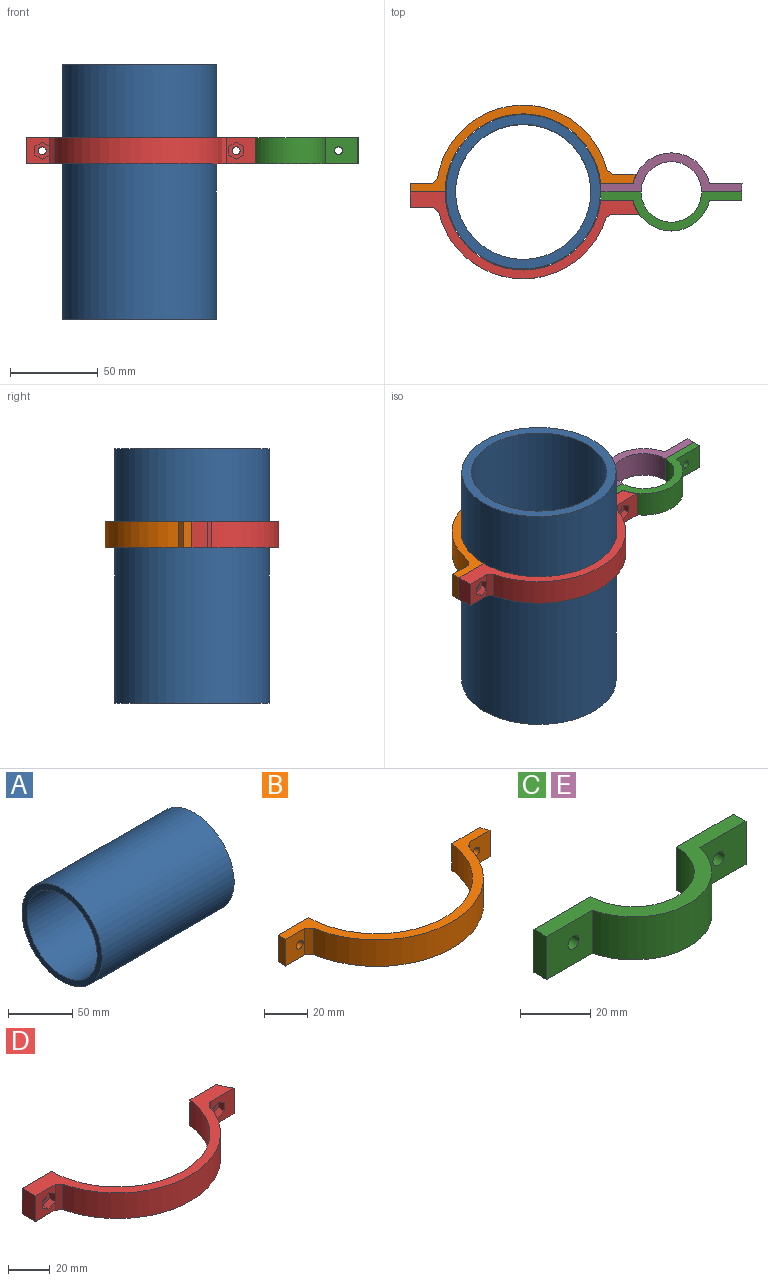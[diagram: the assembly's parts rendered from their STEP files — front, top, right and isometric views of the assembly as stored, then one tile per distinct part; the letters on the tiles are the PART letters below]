
ASSEMBLY  parts=5 mates=6
PART A: 4 faces, bbox 145x88x88 mm
  f0: cylinder r=38.5mm len=145mm, axis (-1,0,0), area 35075.9mm2, adj f2,f3
  f1: cylinder r=44mm len=145mm, axis (-1,0,0), area 40086.7mm2, adj f2,f3
  f2: plane 88x88mm, normal (1,0,0), area 1425.5mm2, adj f0,f1
  f3: plane 88x88mm, normal (-1,0,0), area 1425.5mm2, adj f0,f1
PART B: 14 faces, bbox 128.8x49.5x15 mm
  f0: cylinder r=22.25mm len=15mm, axis (0,0,-1), area 79.9mm2, adj f1,f2,f4,f11
  f1: plane 128.8x49.5mm, normal (0,0,1), area 866.8mm2, adj f0,f4,f5,f6,f7,f8,f9,f11
  f2: plane 128.8x49.5mm, normal (0,0,-1), area 866.8mm2, adj f0,f4,f5,f6,f7,f8,f9,f11
  f3: cylinder r=2.25mm len=5mm, axis (0,1,0), area 70.7mm2, adj f4,f11
  f4: plane 18.28x15mm, normal (0,1,0), area 258.3mm2, adj f0,f1,f2,f3,f5
  f5: cylinder r=44.5mm len=88.72mm, axis (0,0,-1), area 2021.9mm2, adj f1,f2,f4,f6
  f6: plane 20x15mm, normal (0,1,0), area 284.1mm2, adj f1,f2,f5,f7,f10
  f7: plane 15x5mm, normal (-1,0,0), area 75mm2, adj f1,f2,f6,f8
  f8: plane 15x12.55mm, normal (0,-1,0), area 172.4mm2, adj f1,f2,f7,f10,f12
  f9: cylinder r=49.5mm len=96.86mm, axis (0,0,-1), area 2031.7mm2, adj f1,f2,f12,f13
  f10: cylinder r=2.25mm len=5mm, axis (0,1,0), area 70.7mm2, adj f6,f8
  f11: plane 15x13.39mm, normal (0,-1,0), area 184.9mm2, adj f0,f1,f2,f3,f13
  f12: plane 15x3.03mm, normal (-0.65,-0.76,0), area 59.9mm2, adj f1,f2,f8,f9
  f13: plane 15x2.97mm, normal (0.61,-0.79,0), area 56.4mm2, adj f1,f2,f9,f11
PART C: 12 faces, bbox 80.5x22.3x15 mm
  f0: cylinder r=22.25mm len=43.36mm, axis (0,0,-1), area 897.2mm2, adj f1,f7,f8,f9
  f1: plane 18.57x15mm, normal (0,-1,0), area 262.6mm2, adj f0,f2,f8,f9,f11
  f2: cylinder r=89mm len=15mm, axis (0,0,-1), area 75mm2, adj f1,f3,f8,f9
  f3: plane 22.86x15mm, normal (0,1,0), area 327mm2, adj f2,f4,f8,f9,f11
  f4: cylinder r=17.25mm len=34.5mm, axis (0,0,-1), area 812.9mm2, adj f3,f5,f8,f9
  f5: plane 22.86x15mm, normal (0,1,0), area 327mm2, adj f4,f6,f8,f9,f10
  f6: cylinder r=89mm len=15mm, axis (0,0,-1), area 75mm2, adj f5,f7,f8,f9
  f7: plane 18.57x15mm, normal (0,-1,0), area 262.6mm2, adj f0,f6,f8,f9,f10
  f8: plane 80.5x22.25mm, normal (0,0,1), area 491.2mm2, adj f0,f1,f2,f3,f4,f5,f6,f7
  f9: plane 80.5x22.25mm, normal (0,0,-1), area 491.2mm2, adj f0,f1,f2,f3,f4,f5,f6,f7
  f10: cylinder r=2.25mm len=5mm, axis (0,-1,0), area 70.7mm2, adj f5,f7
  f11: cylinder r=2.25mm len=5mm, axis (0,-1,0), area 70.7mm2, adj f1,f3
PART D: 28 faces, bbox 130.6x49.5x15 mm
  f0: plane 9.64x8.35mm, normal (0,-1,0), area 44.5mm2, adj f11,f19,f20,f21,f22,f23,f24
  f1: plane 16.12x15mm, normal (0,-1,0), area 181.4mm2, adj f3,f9,f10,f13,f14,f15,f16,f17
  f2: cylinder r=2.25mm len=4.5mm, axis (0,1,0), area 56.5mm2, adj f4,f12
  f3: cylinder r=22.25mm len=15mm, axis (0,0,-1), area 132.6mm2, adj f1,f4,f9,f10
  f4: plane 18.28x15mm, normal (0,1,0), area 258.3mm2, adj f2,f3,f5,f9,f10
  f5: cylinder r=44.5mm len=88.72mm, axis (0,0,-1), area 2021.9mm2, adj f4,f6,f9,f10
  f6: plane 20x15mm, normal (0,1,0), area 284.1mm2, adj f5,f7,f9,f10,f11
  f7: plane 15x9mm, normal (-1,0,0), area 135mm2, adj f6,f9,f10,f25
  f8: cylinder r=49.5mm len=95.33mm, axis (0,0,-1), area 1931.4mm2, adj f9,f10,f26,f27
  f9: plane 130.62x49.5mm, normal (0,0,1), area 978.8mm2, adj f1,f3,f4,f5,f6,f7,f8,f25
  f10: plane 130.62x49.5mm, normal (0,0,-1), area 978.8mm2, adj f1,f3,f4,f5,f6,f7,f8,f25
  f11: cylinder r=2.25mm len=5mm, axis (0,1,0), area 70.7mm2, adj f0,f6
  f12: plane 9.64x8.35mm, normal (0,-1,0), area 44.5mm2, adj f2,f13,f14,f15,f16,f17,f18
  f13: plane 4.18x4mm, normal (-0.5,0,-0.87), area 19.3mm2, adj f1,f12,f14,f18
  f14: plane 4.18x4mm, normal (0.5,0,-0.87), area 19.3mm2, adj f1,f12,f13,f15
  f15: plane 4.82x4mm, normal (1,0,0), area 19.3mm2, adj f1,f12,f14,f16
  f16: plane 4.18x4mm, normal (0.5,0,0.87), area 19.3mm2, adj f1,f12,f15,f17
  f17: plane 4.18x4mm, normal (-0.5,0,0.87), area 19.3mm2, adj f1,f12,f16,f18
  f18: plane 4.82x4mm, normal (-1,0,0), area 19.3mm2, adj f1,f12,f13,f17
  f19: plane 4.18x4mm, normal (0.5,0,-0.87), area 19.3mm2, adj f0,f20,f24,f25
  f20: plane 4.18x4.02mm, normal (-0.5,0,-0.87), area 19.3mm2, adj f0,f19,f21,f25,f27
  f21: plane 4.82x4.02mm, normal (-1,0,0), area 19.4mm2, adj f0,f20,f22,f27
  f22: plane 4.18x4.02mm, normal (-0.5,0,0.87), area 19.3mm2, adj f0,f21,f23,f25,f27
  f23: plane 4.18x4mm, normal (0.5,0,0.87), area 19.3mm2, adj f0,f22,f24,f25
  f24: plane 4.82x4mm, normal (1,0,0), area 19.3mm2, adj f0,f19,f23,f25
  f25: plane 15x13.39mm, normal (0,-1,0), area 140.5mm2, adj f7,f9,f10,f19,f20,f22,f23,f24
  f26: plane 15x2.86mm, normal (0.59,-0.81,0), area 53.1mm2, adj f1,f8,f9,f10
  f27: plane 15x2.93mm, normal (-0.62,-0.78,0), area 55.8mm2, adj f8,f9,f10,f20,f21,f22,f25
PART E: same geometry as C
PLACE A rot(axis=(0,1,0),90deg) t=(-79.78,-0.5,22.74)mm
PLACE B rot(axis=(1,0,0),180deg) t=(-79.78,-0.5,46.23)mm
PLACE C t=(4.66,-0.5,46.23)mm
PLACE D t=(-79.78,-0.5,46.23)mm
PLACE E rot(axis=(0,0,-1),180deg) t=(4.66,-0.5,46.23)mm
MATE planar E.f3 <-> C.f5  axis (0,-1,0) through (-24,-0.5,46.23)mm
MATE cylindrical D.f2 <-> E.f11  axis (0,1,0) through (-24.52,-7.5,46.23)mm
MATE cylindrical C.f10 <-> D.f2  axis (0,-1,0) through (-24.52,-3,46.23)mm
MATE planar B.f6 <-> D.f6  axis (0,-1,0) through (-134.24,-0.5,46.23)mm
MATE cylindrical D.f5 <-> A.f0  axis (0,0,-1) through (-79.78,-0.5,46.23)mm
MATE planar D.f4 <-> C.f7  axis (0,1,0) through (-26.54,-5.5,46.23)mm
